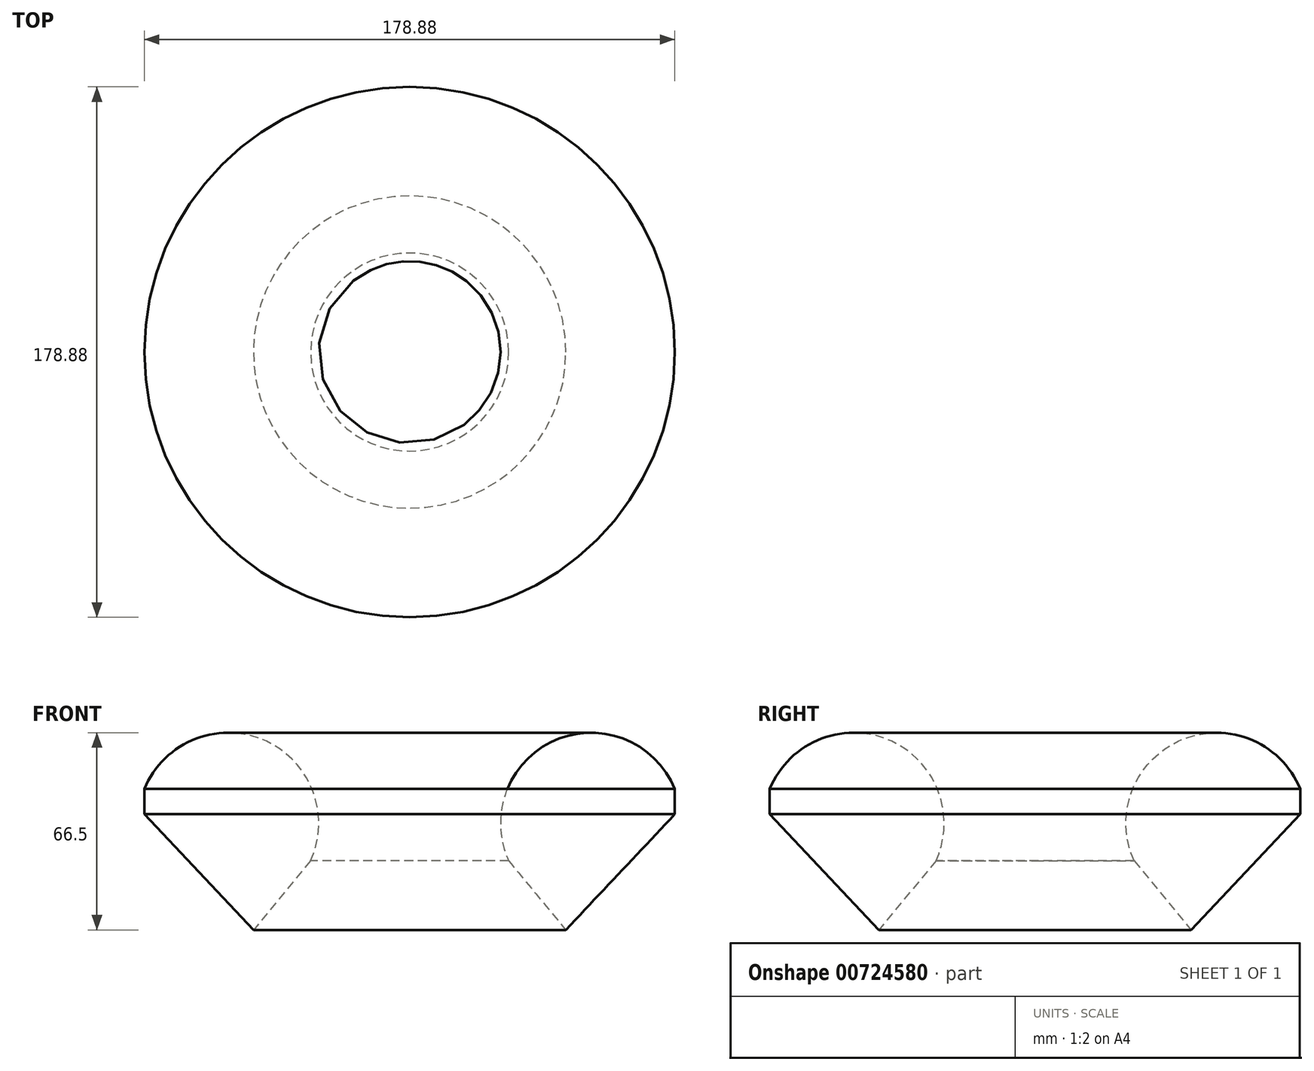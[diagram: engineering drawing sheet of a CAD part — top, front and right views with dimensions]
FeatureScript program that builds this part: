
annotation { "Feature Type Name" : "Feature", "Feature Type Description" : "" }
export const myFeature = defineFeature(function(context is Context, id is Id, definition is map)
    precondition{}
    {
        {
            var Q0;
            Q0=qCreatedBy(makeId("Front.planeOp"),FACE);
            var sketch = newSketch(context, id + "F0", { "sketchPlane" : qUnion([Q0])});
            skLineSegment(sketch, "E0", {"start": v(33.4, -4.03) * mm, "end": v(52.67, -27.34) * mm});
            skLineSegment(sketch, "E1", {"start": v(52.67, -27.34) * mm, "end": v(89.44, 11.68) * mm});
            skLineSegment(sketch, "E2", {"start": v(89.44, 11.68) * mm, "end": v(89.44, 20.23) * mm});
            skArc(sketch, "E3", {"start": v(89.44, 20.23) * mm, "mid": v(49.06, 36.65) * mm, "end": v(33.4, -4.03) * mm});
            skSolve(sketch);
        }
        {
            var Q0;
            Q0=qCreatedBy(makeId("Front.planeOp"),FACE);
            var sketch = newSketch(context, id + "F1", { "sketchPlane" : qUnion([Q0])});
            skLineSegment(sketch, "E4", {"start": v(0, 60.51) * mm, "end": v(0, -53.79) * mm});
            skSolve(sketch);
        }
        {
            var Q0;
            Q0=makeQuery(id+"F0.imprint","IMPRINT",FACE,{"disambiguationData":[TD([[makeQuery(id+"F0.imprint","IMPRINT",EDGE,{"derivedFrom":sQuery(id+"F0.wireOp",EDGE,"E0")}),1.0]])]});
            var Q1;
            Q1=sQuery(id+"F1.wireOp",EDGE,"E4");
            revolve(context, id + "F2", {"surfaceOperationType" : NewSurfaceOperationType.NEW, "entities" : qUnion([Q0]), "axis" : qUnion([Q1]), "revolveType" : RevolveType.FULL});
        }
    });
